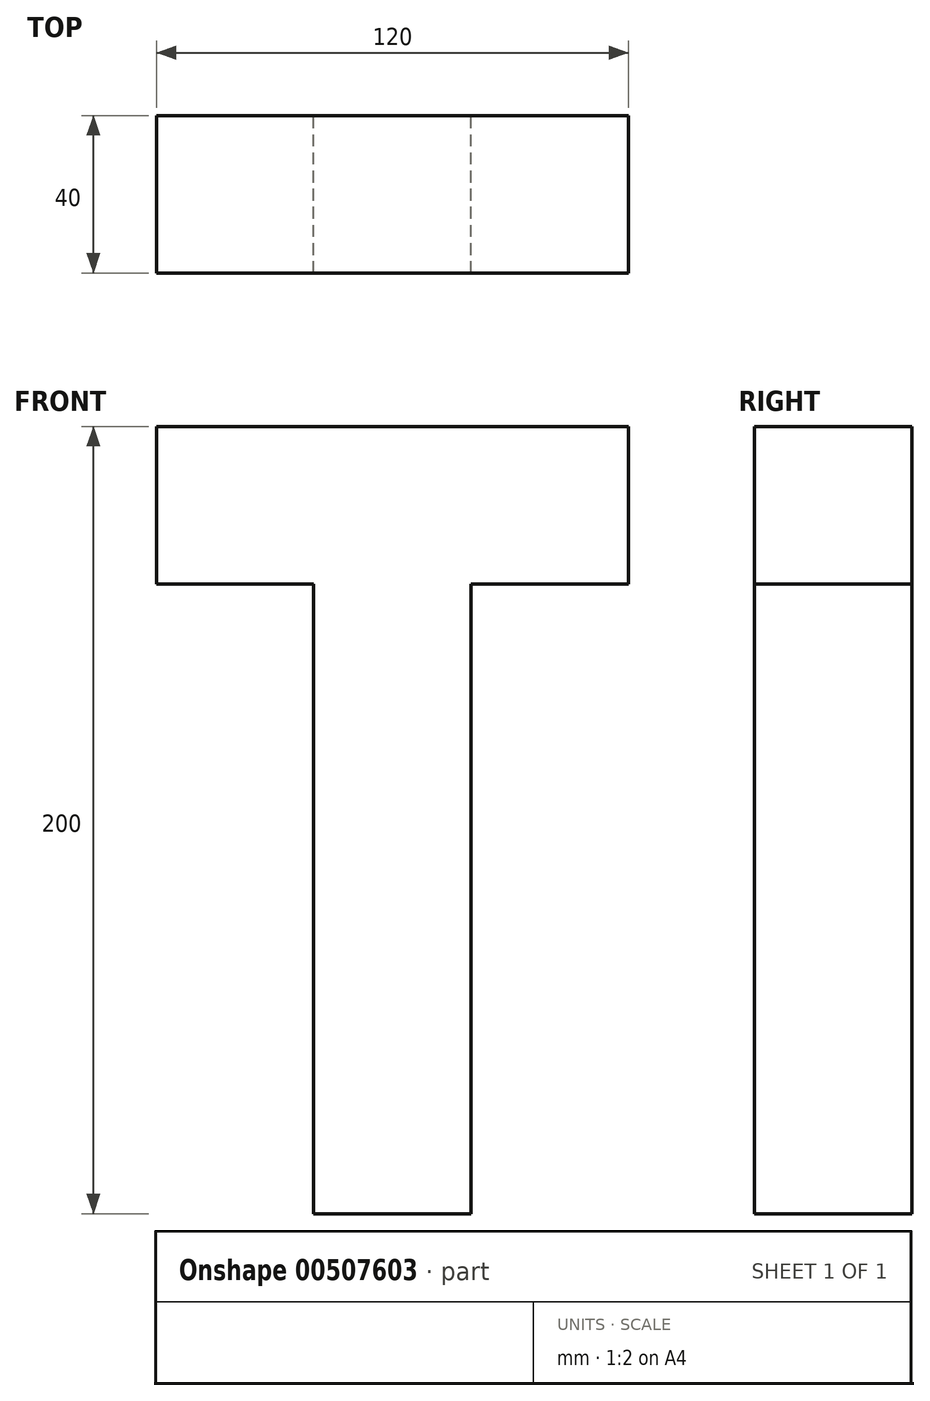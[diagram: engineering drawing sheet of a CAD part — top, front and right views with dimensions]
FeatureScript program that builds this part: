
annotation { "Feature Type Name" : "Feature", "Feature Type Description" : "" }
export const myFeature = defineFeature(function(context is Context, id is Id, definition is map)
    precondition{}
    {
        {
            var Q0;
            Q0=qCreatedBy(makeId("Front.planeOp"),FACE);
            var sketch = newSketch(context, id + "F0", { "sketchPlane" : qUnion([Q0])});
            skLineSegment(sketch, "E0.bottom", {"start": v(60, 100) * mm, "end": v(-60, 100) * mm});
            skLineSegment(sketch, "E0.top", {"start": v(60, -100) * mm, "end": v(-60, -100) * mm});
            skLineSegment(sketch, "E0.left", {"start": v(60, 100) * mm, "end": v(60, -100) * mm});
            skLineSegment(sketch, "E0.right", {"start": v(-60, 100) * mm, "end": v(-60, -100) * mm});
            skPoint(sketch, "E0.middle", {"position": v(0, 0) * mm});
            skLineSegment(sketch, "E1", {"start": v(-20, 100) * mm, "end": v(-20, -100) * mm});
            skLineSegment(sketch, "E2", {"start": v(20, 100) * mm, "end": v(20, -100) * mm});
            skLineSegment(sketch, "E3", {"start": v(60, 60) * mm, "end": v(-60, 60) * mm});
            skLineSegment(sketch, "E4", {"start": v(60, 20) * mm, "end": v(-60, 20) * mm});
            skLineSegment(sketch, "E5", {"start": v(60, -20) * mm, "end": v(-60, -20) * mm});
            skLineSegment(sketch, "E6", {"start": v(60, -60) * mm, "end": v(-60, -60) * mm});
            skSolve(sketch);
        }
        {
            var Q0;
            {var subQ0=sQuery(id+"F0.wireOp",EDGE,"E0.right");var subQ1=sQuery(id+"F0.wireOp",EDGE,"E0.bottom");var subQ2=makeQuery(id+"F0.imprint","INTERSECT",VERTEX,{"derivedFrom":[subQ1,subQ0]});Q0=makeQuery(id+"F0.imprint","IMPRINT",FACE,{"disambiguationData":[TD([[makeQuery(id+"F0.imprint","IMPRINT",EDGE,{"disambiguationData":[TD([[subQ2,1.0]])],"derivedFrom":subQ1}),1.0]])]});}
            var Q1;
            {var subQ0=sQuery(id+"F0.wireOp",EDGE,"E1");var subQ1=sQuery(id+"F0.wireOp",EDGE,"E0.bottom");var subQ2=makeQuery(id+"F0.imprint","INTERSECT",VERTEX,{"derivedFrom":[subQ1,subQ0]});Q1=makeQuery(id+"F0.imprint","IMPRINT",FACE,{"disambiguationData":[TD([[makeQuery(id+"F0.imprint","IMPRINT",EDGE,{"disambiguationData":[TD([[subQ2,1.0]])],"derivedFrom":subQ1}),1.0]])]});}
            var Q2;
            {var subQ0=sQuery(id+"F0.wireOp",EDGE,"E0.left");var subQ1=sQuery(id+"F0.wireOp",EDGE,"E0.bottom");var subQ2=makeQuery(id+"F0.imprint","INTERSECT",VERTEX,{"derivedFrom":[subQ1,subQ0]});Q2=makeQuery(id+"F0.imprint","IMPRINT",FACE,{"disambiguationData":[TD([[makeQuery(id+"F0.imprint","IMPRINT",EDGE,{"disambiguationData":[TD([[subQ2,-1.0]])],"derivedFrom":subQ1}),1.0]])]});}
            var Q3;
            {var subQ0=sQuery(id+"F0.wireOp",EDGE,"E3");var subQ1=sQuery(id+"F0.wireOp",EDGE,"E1");var subQ2=makeQuery(id+"F0.imprint","INTERSECT",VERTEX,{"derivedFrom":[subQ1,subQ0]});Q3=makeQuery(id+"F0.imprint","IMPRINT",FACE,{"disambiguationData":[TD([[makeQuery(id+"F0.imprint","IMPRINT",EDGE,{"disambiguationData":[TD([[subQ2,-1.0]])],"derivedFrom":subQ1}),1.0]])]});}
            var Q4;
            {var subQ0=sQuery(id+"F0.wireOp",EDGE,"E4");var subQ1=sQuery(id+"F0.wireOp",EDGE,"E1");var subQ2=makeQuery(id+"F0.imprint","INTERSECT",VERTEX,{"derivedFrom":[subQ1,subQ0]});Q4=makeQuery(id+"F0.imprint","IMPRINT",FACE,{"disambiguationData":[TD([[makeQuery(id+"F0.imprint","IMPRINT",EDGE,{"disambiguationData":[TD([[subQ2,-1.0]])],"derivedFrom":subQ1}),1.0]])]});}
            var Q5;
            {var subQ0=sQuery(id+"F0.wireOp",EDGE,"E5");var subQ1=sQuery(id+"F0.wireOp",EDGE,"E1");var subQ2=makeQuery(id+"F0.imprint","INTERSECT",VERTEX,{"derivedFrom":[subQ1,subQ0]});Q5=makeQuery(id+"F0.imprint","IMPRINT",FACE,{"disambiguationData":[TD([[makeQuery(id+"F0.imprint","IMPRINT",EDGE,{"disambiguationData":[TD([[subQ2,-1.0]])],"derivedFrom":subQ1}),1.0]])]});}
            var Q6;
            {var subQ0=sQuery(id+"F0.wireOp",EDGE,"E1");var subQ1=sQuery(id+"F0.wireOp",EDGE,"E0.top");var subQ2=makeQuery(id+"F0.imprint","INTERSECT",VERTEX,{"derivedFrom":[subQ1,subQ0]});Q6=makeQuery(id+"F0.imprint","IMPRINT",FACE,{"disambiguationData":[TD([[makeQuery(id+"F0.imprint","IMPRINT",EDGE,{"disambiguationData":[TD([[subQ2,1.0]])],"derivedFrom":subQ1}),-1.0]])]});}
            extrude(context, id + "F1", {"entities" : qUnion([Q0, Q1, Q2, Q3, Q4, Q5, Q6]), "depth" : 40 * mm, "offsetDistance" : 25 * mm});
        }
    });
